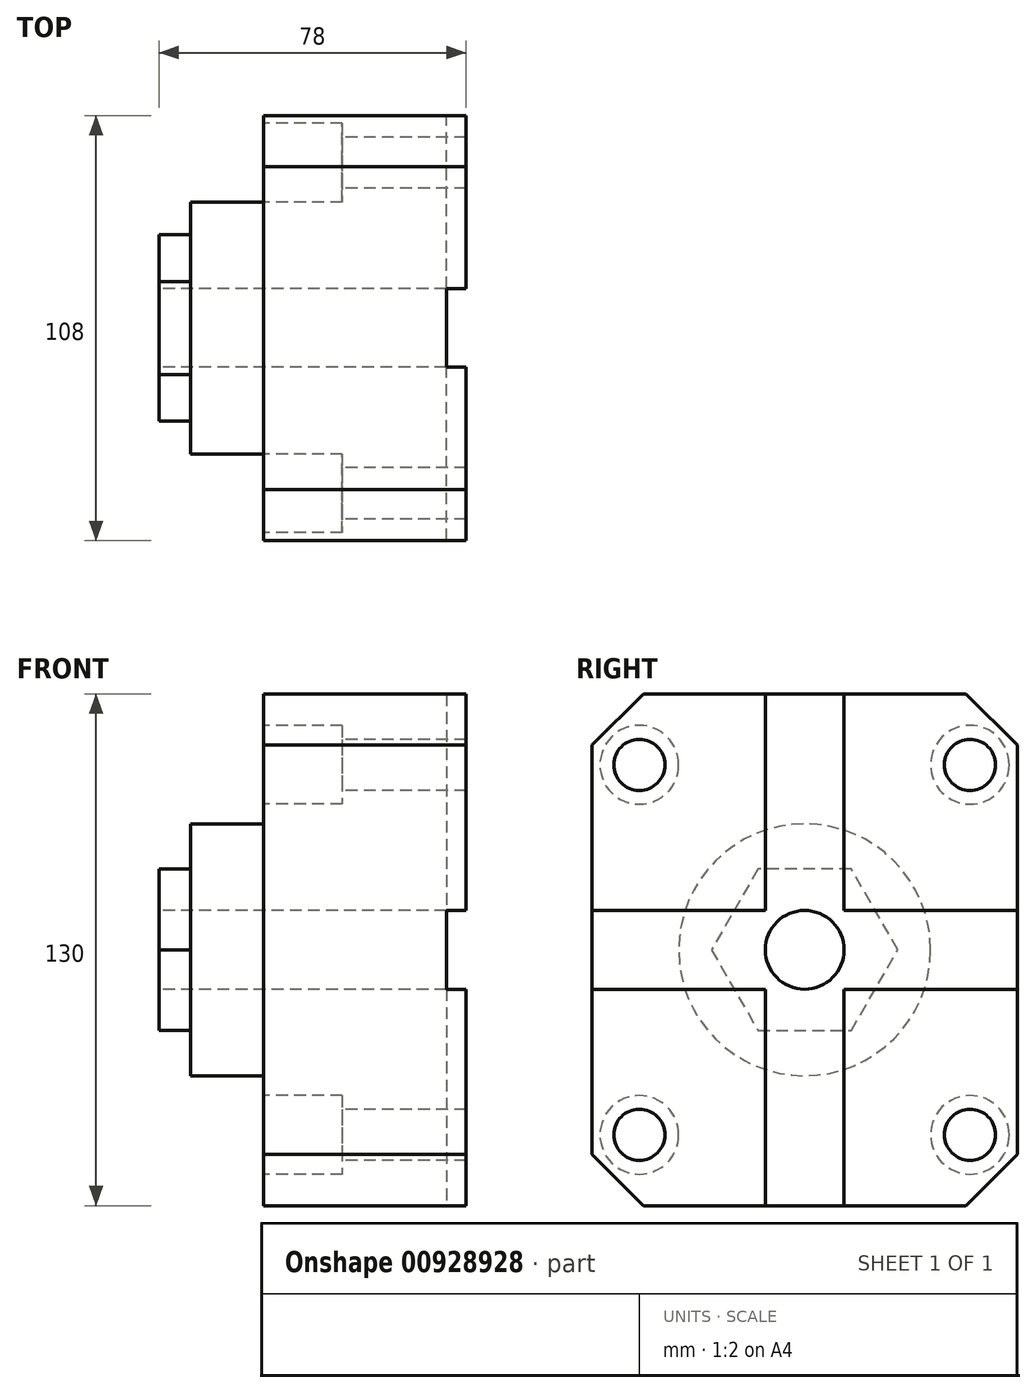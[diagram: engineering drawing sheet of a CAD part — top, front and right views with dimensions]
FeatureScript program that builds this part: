
annotation { "Feature Type Name" : "Feature", "Feature Type Description" : "" }
export const myFeature = defineFeature(function(context is Context, id is Id, definition is map)
    precondition{}
    {
        {
            var Q0;
            Q0=qCreatedBy(makeId("Right.planeOp"),FACE);
            var sketch = newSketch(context, id + "F0", { "sketchPlane" : qUnion([Q0])});
            skLineSegment(sketch, "E0.bottom", {"start": v(54, 65) * mm, "end": v(-54, 65) * mm});
            skLineSegment(sketch, "E0.top", {"start": v(54, -65) * mm, "end": v(-54, -65) * mm});
            skLineSegment(sketch, "E0.left", {"start": v(54, 65) * mm, "end": v(54, -65) * mm});
            skLineSegment(sketch, "E0.right", {"start": v(-54, 65) * mm, "end": v(-54, -65) * mm});
            skPoint(sketch, "E0.middle", {"position": v(0, 0) * mm});
            skSolve(sketch);
        }
        {
            var Q0;
            Q0=makeQuery(id+"F0.imprint","IMPRINT",FACE,{"disambiguationData":[TD([[makeQuery(id+"F0.imprint","IMPRINT",EDGE,{"derivedFrom":sQuery(id+"F0.wireOp",EDGE,"E0.bottom")}),1.0]])]});
            extrude(context, id + "F1", {"entities" : qUnion([Q0]), "oppositeDirection" : true, "depth" : 51.5 * mm, "offsetDistance" : 25 * mm});
        }
        {
            var Q0;
            Q0=makeQuery(id+"F1.opExtrude","CAP_FACE",FACE,{"disambiguationData":[OSD([sQuery(id+"F0.wireOp",EDGE,"E0.bottom"),sQuery(id+"F0.wireOp",EDGE,"E0.top"),sQuery(id+"F0.wireOp",EDGE,"E0.left"),sQuery(id+"F0.wireOp",EDGE,"E0.right")])],"isStart":false});
            var sketch = newSketch(context, id + "F2", { "sketchPlane" : qUnion([Q0])});
            skCircle(sketch, "E1", {"center": v(42, 47) * mm, "radius": 6.5 * mm});
            skCircle(sketch, "E2.MirrorC", {"center": v(-42, 47) * mm, "radius": 6.5 * mm});
            skCircle(sketch, "E3.MirrorC", {"center": v(-42, -47) * mm, "radius": 6.5 * mm});
            skCircle(sketch, "E4.MirrorC", {"center": v(42, -47) * mm, "radius": 6.5 * mm});
            skSolve(sketch);
        }
        {
            var Q0;
            Q0 = qSketchRegion(id + "F2", true);
            extrude(context, id + "F3", {"entities" : qUnion([Q0]), "operationType" : NewBodyOperationType.REMOVE, "endBound" : BoundingType.THROUGH_ALL, "oppositeDirection" : true, "depth" : 25 * mm, "offsetDistance" : 25 * mm});
        }
        {
            var Q0;
            Q0=makeQuery(id+"F1.opExtrude","CAP_FACE",FACE,{"disambiguationData":[OSD([sQuery(id+"F0.wireOp",EDGE,"E0.bottom"),sQuery(id+"F0.wireOp",EDGE,"E0.top"),sQuery(id+"F0.wireOp",EDGE,"E0.left"),sQuery(id+"F0.wireOp",EDGE,"E0.right")])],"isStart":false});
            var sketch = newSketch(context, id + "F4", { "sketchPlane" : qUnion([Q0])});
            skCircle(sketch, "E5", {"center": v(-42, 47) * mm, "radius": 10 * mm});
            skCircle(sketch, "E6.0.1.0", {"center": v(-42, -47) * mm, "radius": 10 * mm});
            skCircle(sketch, "E6.1.0.0", {"center": v(42, 47) * mm, "radius": 10 * mm});
            skCircle(sketch, "E6.1.1.0", {"center": v(42, -47) * mm, "radius": 10 * mm});
            skLineSegment(sketch, "E6.direction1", {"start": v(-42, 47) * mm, "end": v(42, 47) * mm, "construction": true});
            skLineSegment(sketch, "E6.direction2", {"start": v(-42, 47) * mm, "end": v(-42, -47) * mm, "construction": true});
            skSolve(sketch);
        }
        {
            var Q0;
            Q0 = qSketchRegion(id + "F4", true);
            extrude(context, id + "F5", {"entities" : qUnion([Q0]), "operationType" : NewBodyOperationType.REMOVE, "oppositeDirection" : true, "depth" : 20 * mm, "offsetDistance" : 25 * mm});
        }
        {
            var Q0;
            Q0=qCreatedBy(makeId("Right.planeOp"),FACE);
            cPlane(context, id + "F6", {"entities" : qUnion([Q0]), "cplaneType" : CPlaneType.OFFSET, "offset" : 70 * mm, "oppositeDirection" : true, "width" : 150 * mm, "height" : 150 * mm});
        }
        {
            var Q0;
            Q0=qCreatedBy(id+"F6.planeOp",FACE);
            var sketch = newSketch(context, id + "F7", { "sketchPlane" : qUnion([Q0])});
            skCircle(sketch, "E7", {"center": v(0, 0) * mm, "radius": 32 * mm});
            skSolve(sketch);
        }
        {
            var Q0;
            Q0 = qSketchRegion(id + "F7", true);
            extrude(context, id + "F8", {"entities" : qUnion([Q0]), "operationType" : NewBodyOperationType.ADD, "endBound" : BoundingType.UP_TO_NEXT, "depth" : 25 * mm, "offsetDistance" : 25 * mm});
        }
        {
            var Q0;
            Q0=makeQuery(id+"F8.opExtrude","CAP_FACE",FACE,{"disambiguationData":[OSD([sQuery(id+"F7.wireOp",EDGE,"E7")])],"isStart":true});
            var sketch = newSketch(context, id + "F9", { "sketchPlane" : qUnion([Q0])});
            skCircle(sketch, "E8.cCircle", {"center": v(0, 0) * mm, "radius": 20.5 * mm, "construction": true});
            skLineSegment(sketch, "E8.0", {"start": v(11.84, 20.5) * mm, "end": v(23.67, 0) * mm});
            skLineSegment(sketch, "E8.1", {"start": v(23.67, 0) * mm, "end": v(11.84, -20.5) * mm});
            skLineSegment(sketch, "E8.2", {"start": v(11.84, -20.5) * mm, "end": v(-11.84, -20.5) * mm});
            skLineSegment(sketch, "E8.3", {"start": v(-11.84, -20.5) * mm, "end": v(-23.67, 0) * mm});
            skLineSegment(sketch, "E8.4", {"start": v(-23.67, 0) * mm, "end": v(-11.84, 20.5) * mm});
            skLineSegment(sketch, "E8.5", {"start": v(-11.84, 20.5) * mm, "end": v(11.84, 20.5) * mm});
            skPoint(sketch, "E8.0.midPoint", {"position": v(17.75, 10.25) * mm});
            skSolve(sketch);
        }
        {
            var Q0;
            Q0 = qSketchRegion(id + "F9", true);
            extrude(context, id + "F10", {"entities" : qUnion([Q0]), "operationType" : NewBodyOperationType.ADD, "depth" : 8 * mm, "offsetDistance" : 25 * mm});
        }
        {
            var Q0;
            Q0=makeQuery(id+"F10.opExtrude","CAP_FACE",FACE,{"disambiguationData":[OSD([sQuery(id+"F9.wireOp",EDGE,"E8.0"),sQuery(id+"F9.wireOp",EDGE,"E8.1"),sQuery(id+"F9.wireOp",EDGE,"E8.2"),sQuery(id+"F9.wireOp",EDGE,"E8.3"),sQuery(id+"F9.wireOp",EDGE,"E8.4"),sQuery(id+"F9.wireOp",EDGE,"E8.5")])],"isStart":false});
            var sketch = newSketch(context, id + "F11", { "sketchPlane" : qUnion([Q0])});
            skCircle(sketch, "E9", {"center": v(0, 0) * mm, "radius": 10 * mm});
            skSolve(sketch);
        }
        {
            var Q0;
            Q0 = qSketchRegion(id + "F11", true);
            extrude(context, id + "F12", {"entities" : qUnion([Q0]), "operationType" : NewBodyOperationType.REMOVE, "endBound" : BoundingType.THROUGH_ALL, "oppositeDirection" : true, "depth" : 25 * mm, "offsetDistance" : 25 * mm});
        }
        {
            var Q0;
            Q0=makeQuery(id+"F1.opExtrude","SWEPT_EDGE",EDGE,{"disambiguationData":[OSD([sQuery(id+"F0.wireOp",EDGE,"E0.bottom"),sQuery(id+"F0.wireOp",EDGE,"E0.right")])]});
            var Q1;
            Q1=makeQuery(id+"F1.opExtrude","SWEPT_EDGE",EDGE,{"disambiguationData":[OSD([sQuery(id+"F0.wireOp",EDGE,"E0.bottom"),sQuery(id+"F0.wireOp",EDGE,"E0.left")])]});
            var Q2;
            Q2=makeQuery(id+"F1.opExtrude","SWEPT_EDGE",EDGE,{"disambiguationData":[OSD([sQuery(id+"F0.wireOp",EDGE,"E0.top"),sQuery(id+"F0.wireOp",EDGE,"E0.right")])]});
            var Q3;
            Q3=makeQuery(id+"F1.opExtrude","SWEPT_EDGE",EDGE,{"disambiguationData":[OSD([sQuery(id+"F0.wireOp",EDGE,"E0.top"),sQuery(id+"F0.wireOp",EDGE,"E0.left")])]});
            chamfer(context, id + "F13", {"entities" : qUnion([Q0, Q1, Q2, Q3]), "width" : 13 * mm, "tangentPropagation" : true});
        }
        {
            var Q0;
            Q0=makeQuery(id+"F1.opExtrude","CAP_FACE",FACE,{"disambiguationData":[OSD([sQuery(id+"F0.wireOp",EDGE,"E0.bottom"),sQuery(id+"F0.wireOp",EDGE,"E0.top"),sQuery(id+"F0.wireOp",EDGE,"E0.left"),sQuery(id+"F0.wireOp",EDGE,"E0.right")])],"isStart":true});
            var sketch = newSketch(context, id + "F14", { "sketchPlane" : qUnion([Q0])});
            skLineSegment(sketch, "E10.bottom", {"start": v(-10, 65) * mm, "end": v(10, 65) * mm});
            skLineSegment(sketch, "E10.top", {"start": v(-10, -65) * mm, "end": v(10, -65) * mm});
            skLineSegment(sketch, "E10.left", {"start": v(-10, 65) * mm, "end": v(-10, -65) * mm});
            skLineSegment(sketch, "E10.right", {"start": v(10, 65) * mm, "end": v(10, -65) * mm});
            skPoint(sketch, "E10.middle", {"position": v(0, 0) * mm});
            skLineSegment(sketch, "E11.bottom", {"start": v(-54, 10) * mm, "end": v(54, 10) * mm});
            skLineSegment(sketch, "E11.top", {"start": v(-54, -10) * mm, "end": v(54, -10) * mm});
            skLineSegment(sketch, "E11.left", {"start": v(-54, 10) * mm, "end": v(-54, -10) * mm});
            skLineSegment(sketch, "E11.right", {"start": v(54, 10) * mm, "end": v(54, -10) * mm});
            skSolve(sketch);
        }
        {
            var Q0;
            Q0 = qSketchRegion(id + "F14", true);
            extrude(context, id + "F15", {"entities" : qUnion([Q0]), "operationType" : NewBodyOperationType.REMOVE, "oppositeDirection" : true, "depth" : 5 * mm, "offsetDistance" : 25 * mm});
        }
    });
